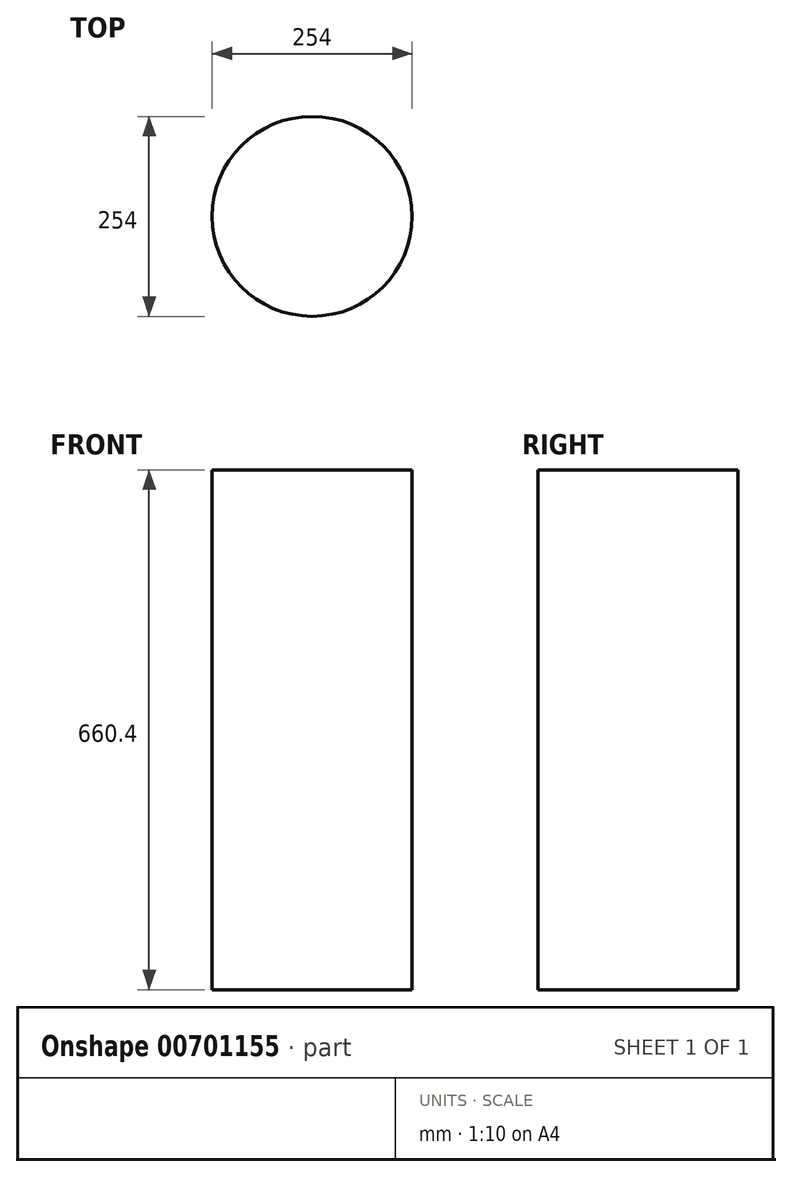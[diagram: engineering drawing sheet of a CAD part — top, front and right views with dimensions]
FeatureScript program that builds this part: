
annotation { "Feature Type Name" : "Feature", "Feature Type Description" : "" }
export const myFeature = defineFeature(function(context is Context, id is Id, definition is map)
    precondition{}
    {
        {
            var Q0;
            Q0=qCreatedBy(makeId("Top.planeOp"),FACE);
            var sketch = newSketch(context, id + "F0", { "sketchPlane" : qUnion([Q0])});
            skCircle(sketch, "E0", {"center": v(0, 0) * mm, "radius": 127 * mm});
            skSolve(sketch);
        }
        {
            var Q0;
            Q0 = qSketchRegion(id + "F0", true);
            extrude(context, id + "F1", {"entities" : qUnion([Q0]), "depth" : 660.4 * mm, "offsetDistance" : 25.4 * mm});
        }
    });
